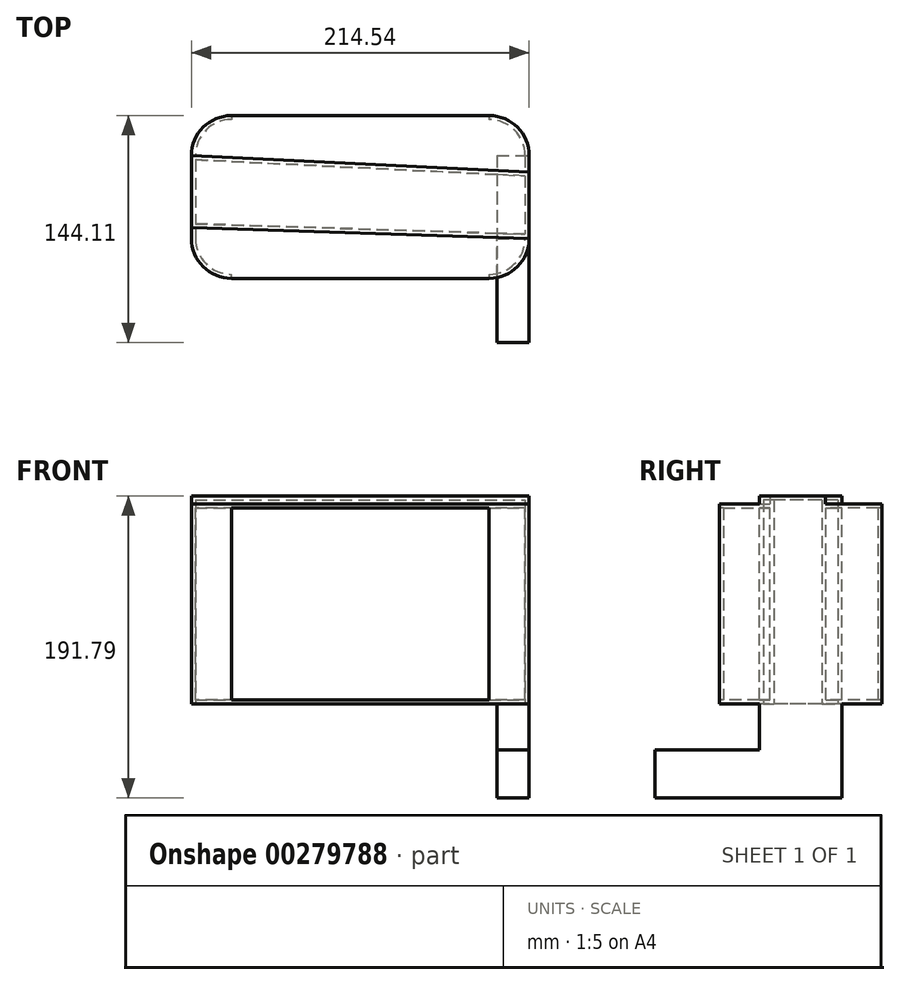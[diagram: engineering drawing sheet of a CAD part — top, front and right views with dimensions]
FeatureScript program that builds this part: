
annotation { "Feature Type Name" : "Feature", "Feature Type Description" : "" }
export const myFeature = defineFeature(function(context is Context, id is Id, definition is map)
    precondition{}
    {
        {
            var Q0;
            Q0=qCreatedBy(makeId("Top.planeOp"),FACE);
            var sketch = newSketch(context, id + "F0", { "sketchPlane" : qUnion([Q0])});
            skLineSegment(sketch, "E0.bottom", {"start": v(0, 0) * mm, "end": v(-4.6, 0) * mm});
            skLineSegment(sketch, "E0.top", {"start": v(0, 0) * mm, "end": v(-4.6, 0) * mm});
            skLineSegment(sketch, "E0.left", {"start": v(0, 0) * mm, "end": v(0, 0) * mm});
            skLineSegment(sketch, "E0.right", {"start": v(-4.6, 0) * mm, "end": v(-4.6, 0) * mm});
            skLineSegment(sketch, "E1.bottom", {"start": v(-31.08, 49.25) * mm, "end": v(132.66, 49.25) * mm});
            skLineSegment(sketch, "E1.top", {"start": v(-31.08, -54.1) * mm, "end": v(132.66, -54.1) * mm});
            skLineSegment(sketch, "E1.left", {"start": v(-56.48, 23.85) * mm, "end": v(-56.48, -28.7) * mm});
            skLineSegment(sketch, "E1.right", {"start": v(158.06, 23.85) * mm, "end": v(158.06, -28.7) * mm});
            skPoint(sketch, "E2.visualSharp", {"position": v(-56.48, 49.25) * mm});
            skArc(sketch, "E2.filletArc", {"start": v(-31.08, 49.25) * mm, "mid": v(-49.04, 41.8) * mm, "end": v(-56.48, 23.85) * mm});
            skPoint(sketch, "E3.visualSharp", {"position": v(158.06, 49.25) * mm});
            skArc(sketch, "E3.filletArc", {"start": v(158.06, 23.85) * mm, "mid": v(150.62, 41.8) * mm, "end": v(132.66, 49.25) * mm});
            skPoint(sketch, "E4.visualSharp", {"position": v(158.06, -54.1) * mm});
            skArc(sketch, "E4.filletArc", {"start": v(132.66, -54.1) * mm, "mid": v(150.62, -46.67) * mm, "end": v(158.06, -28.7) * mm});
            skPoint(sketch, "E5.visualSharp", {"position": v(-56.48, -54.1) * mm});
            skArc(sketch, "E5.filletArc", {"start": v(-56.48, -28.7) * mm, "mid": v(-49.04, -46.67) * mm, "end": v(-31.08, -54.1) * mm});
            skLineSegment(sketch, "E6", {"start": v(158.06, 23.85) * mm, "end": v(-56.48, 23.85) * mm});
            skLineSegment(sketch, "E7", {"start": v(-56.48, -28.7) * mm, "end": v(158.06, -28.7) * mm});
            skLineSegment(sketch, "E8", {"start": v(-56.48, -2.43) * mm, "end": v(158.06, -3.43) * mm});
            skSolve(sketch);
        }
        {
            var Q0;
            Q0 = qSketchRegion(id + "F0", true);
            extrude(context, id + "F1", {"entities" : qUnion([Q0]), "depth" : 127 * mm});
        }
        {
            var Q0;
            Q0=makeQuery(id+"F1.opExtrude","SWEPT_FACE",FACE,{"disambiguationData":[OSD([sQuery(id+"F0.wireOp",EDGE,"E1.top")])]});
            shell(context, id + "F2", {"entities" : qUnion([Q0]), "thickness" : 2.54 * mm});
        }
        {
            var Q0;
            Q0=makeQuery(id+"F2.opShell","OFFSET_FACE",FACE,{"disambiguationData":[OSD([sQuery(id+"F0.wireOp",EDGE,"E1.bottom")])]});
            extrude(context, id + "F3", {"entities" : qUnion([Q0]), "operationType" : NewBodyOperationType.REMOVE, "oppositeDirection" : true, "depth" : 25.4 * mm});
        }
        {
            var Q0;
            Q0=makeQuery(id+"F1.opExtrude","CAP_FACE",FACE,{"disambiguationData":[OSD([sQuery(id+"F0.wireOp",EDGE,"E1.bottom"),sQuery(id+"F0.wireOp",EDGE,"E1.top"),sQuery(id+"F0.wireOp",EDGE,"E1.left"),sQuery(id+"F0.wireOp",EDGE,"E1.right"),sQuery(id+"F0.wireOp",EDGE,"E2.filletArc"),sQuery(id+"F0.wireOp",EDGE,"E3.filletArc"),sQuery(id+"F0.wireOp",EDGE,"E4.filletArc"),sQuery(id+"F0.wireOp",EDGE,"E5.filletArc")])],"isStart":true});
            var sketch = newSketch(context, id + "F4", { "sketchPlane" : qUnion([Q0])});
            skLineSegment(sketch, "E9", {"start": v(-56.48, 21.96) * mm, "end": v(158.06, 28.7) * mm});
            skLineSegment(sketch, "E10", {"start": v(-56.48, -23.85) * mm, "end": v(158.06, -13.39) * mm});
            skSolve(sketch);
        }
        {
            var Q0;
            Q0 = qSketchRegion(id + "F4", true);
            var Q1;
            {var subQ0=sQuery(id+"F4.wireOp",EDGE,"E9");Q1=makeQuery(id+"F4.imprint","IMPRINT",FACE,{"disambiguationData":[TD([[makeQuery(id+"F4.imprint","IMPRINT",EDGE,{"derivedFrom":subQ0}),-1.0]])]});}
            extrude(context, id + "F5", {"entities" : qUnion([Q0, Q1]), "operationType" : NewBodyOperationType.ADD, "oppositeDirection" : true, "depth" : 132.08 * mm});
        }
        {
            var Q0;
            Q0=makeQuery(id+"F1.opExtrude","CAP_FACE",FACE,{"disambiguationData":[OSD([sQuery(id+"F0.wireOp",EDGE,"E1.bottom"),sQuery(id+"F0.wireOp",EDGE,"E1.top"),sQuery(id+"F0.wireOp",EDGE,"E1.left"),sQuery(id+"F0.wireOp",EDGE,"E1.right"),sQuery(id+"F0.wireOp",EDGE,"E2.filletArc"),sQuery(id+"F0.wireOp",EDGE,"E3.filletArc"),sQuery(id+"F0.wireOp",EDGE,"E4.filletArc"),sQuery(id+"F0.wireOp",EDGE,"E5.filletArc")])],"isStart":true});
            shell(context, id + "F6", {"entities" : qUnion([Q0]), "thickness" : 2.54 * mm});
        }
        {
            var Q0;
            {var subQ0=sQuery(id+"F0.wireOp",EDGE,"E1.right");Q0=makeQuery(id+"F5.boolean.opBoolean","MERGE",FACE,{"derivedFrom":[makeQuery(id+"F1.opExtrude","SWEPT_FACE",FACE,{"disambiguationData":[OSD([subQ0])]}),makeQuery(id+"F5.opExtrude","SWEPT_FACE",FACE,{"disambiguationData":[OSD([subQ0])]})]});}
            var sketch = newSketch(context, id + "F7", { "sketchPlane" : qUnion([Q0])});
            skLineSegment(sketch, "E11", {"start": v(23.85, 0) * mm, "end": v(23.85, -59.71) * mm});
            skLineSegment(sketch, "E12", {"start": v(23.85, -59.71) * mm, "end": v(-94.86, -59.71) * mm});
            skLineSegment(sketch, "E13", {"start": v(-94.86, -59.71) * mm, "end": v(-94.86, -29.3) * mm});
            skLineSegment(sketch, "E14", {"start": v(-94.86, -29.3) * mm, "end": v(-28.7, -29.3) * mm});
            skLineSegment(sketch, "E15", {"start": v(-28.7, -29.3) * mm, "end": v(-28.7, 0) * mm});
            skSolve(sketch);
        }
        {
            var Q0;
            Q0=makeQuery(id+"F7.imprint","IMPRINT",FACE,{"disambiguationData":[TD([[makeQuery(id+"F7.imprint","IMPRINT",EDGE,{"derivedFrom":sQuery(id+"F7.wireOp",EDGE,"E11")}),-1.0]])]});
            extrude(context, id + "F8", {"entities" : qUnion([Q0]), "operationType" : NewBodyOperationType.ADD, "oppositeDirection" : true, "depth" : 20.32 * mm});
        }
    });
